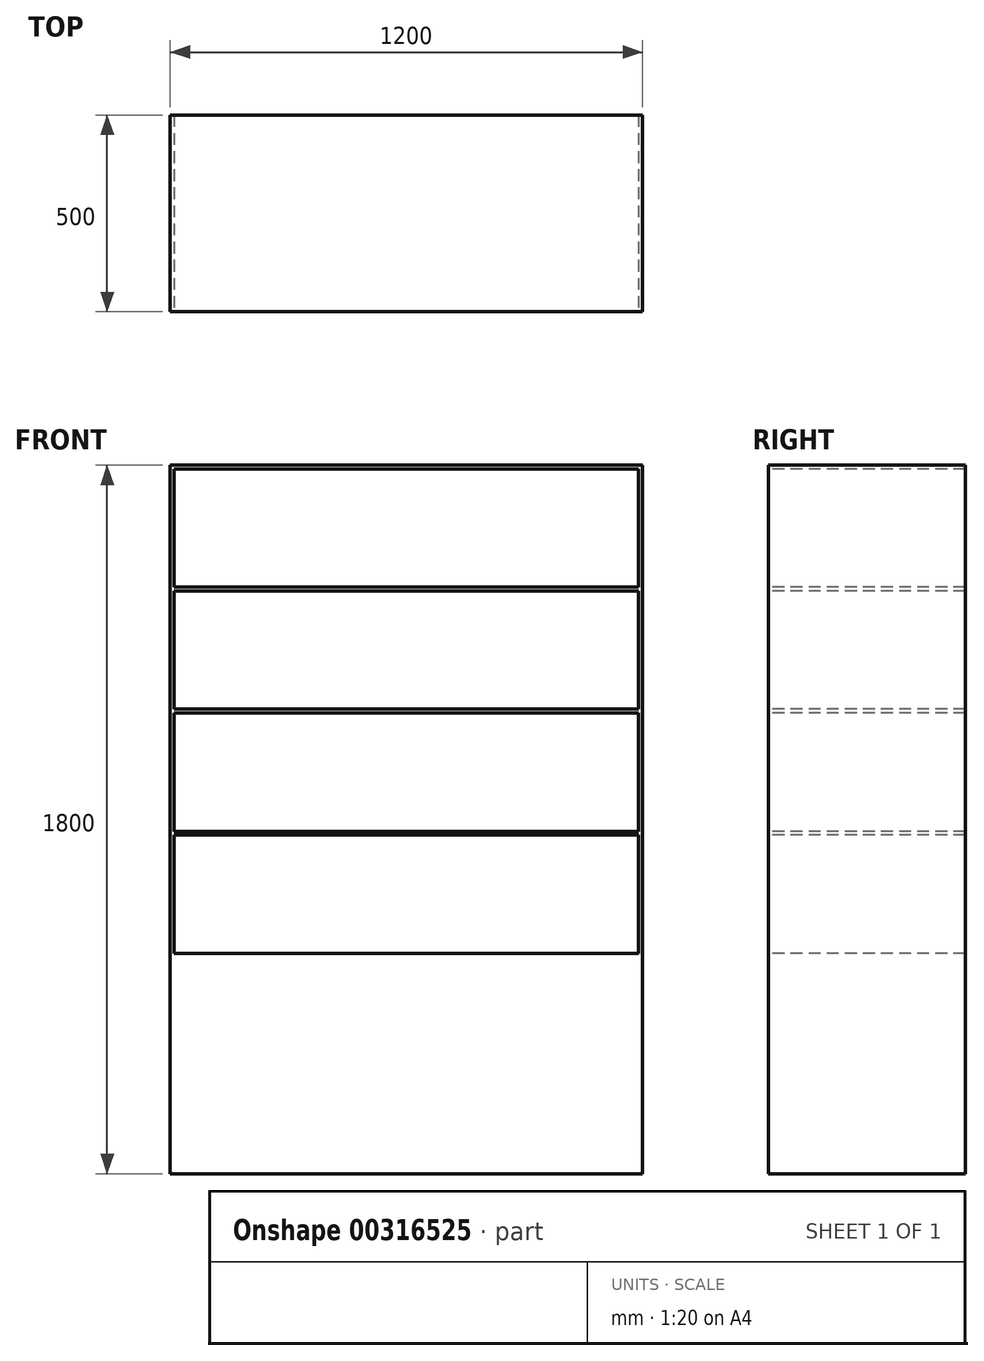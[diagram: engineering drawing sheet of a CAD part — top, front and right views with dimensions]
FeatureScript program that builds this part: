
annotation { "Feature Type Name" : "Feature", "Feature Type Description" : "" }
export const myFeature = defineFeature(function(context is Context, id is Id, definition is map)
    precondition{}
    {
        {
            var Q0;
            Q0=qCreatedBy(makeId("Front.planeOp"),FACE);
            var sketch = newSketch(context, id + "F0", { "sketchPlane" : qUnion([Q0])});
            skLineSegment(sketch, "E0.bottom", {"start": v(-1200, 1800) * mm, "end": v(0, 1800) * mm});
            skLineSegment(sketch, "E0.top", {"start": v(-1200, 0) * mm, "end": v(0, 0) * mm});
            skLineSegment(sketch, "E0.left", {"start": v(-1200, 1800) * mm, "end": v(-1200, 0) * mm});
            skLineSegment(sketch, "E0.right", {"start": v(0, 1800) * mm, "end": v(0, 0) * mm});
            skSolve(sketch);
        }
        {
            var Q0;
            Q0 = qSketchRegion(id + "F0", true);
            extrude(context, id + "F1", {"entities" : qUnion([Q0]), "depth" : 500 * mm});
        }
        {
            var Q0;
            Q0=makeQuery(id+"F1.opExtrude","CAP_FACE",FACE,{"disambiguationData":[OSD([sQuery(id+"F0.wireOp",EDGE,"E0.bottom"),sQuery(id+"F0.wireOp",EDGE,"E0.top"),sQuery(id+"F0.wireOp",EDGE,"E0.left"),sQuery(id+"F0.wireOp",EDGE,"E0.right")])],"isStart":false});
            var sketch = newSketch(context, id + "F2", { "sketchPlane" : qUnion([Q0])});
            skLineSegment(sketch, "E1.bottom", {"start": v(-1190, 1790) * mm, "end": v(-10, 1790) * mm});
            skLineSegment(sketch, "E1.top", {"start": v(-1190, 1490) * mm, "end": v(-10, 1490) * mm});
            skLineSegment(sketch, "E1.left", {"start": v(-1190, 1790) * mm, "end": v(-1190, 1490) * mm});
            skLineSegment(sketch, "E1.right", {"start": v(-10, 1790) * mm, "end": v(-10, 1490) * mm});
            skLineSegment(sketch, "E2.bottom", {"start": v(-1190, 1480) * mm, "end": v(-10, 1480) * mm});
            skLineSegment(sketch, "E2.top", {"start": v(-1190, 1180) * mm, "end": v(-10, 1180) * mm});
            skLineSegment(sketch, "E2.left", {"start": v(-1190, 1480) * mm, "end": v(-1190, 1180) * mm});
            skLineSegment(sketch, "E2.right", {"start": v(-10, 1480) * mm, "end": v(-10, 1180) * mm});
            skLineSegment(sketch, "E3.bottom", {"start": v(-1190, 1170) * mm, "end": v(-10, 1170) * mm});
            skLineSegment(sketch, "E3.top", {"start": v(-1190, 870) * mm, "end": v(-10, 870) * mm});
            skLineSegment(sketch, "E3.left", {"start": v(-1190, 1170) * mm, "end": v(-1190, 870) * mm});
            skLineSegment(sketch, "E3.right", {"start": v(-10, 1170) * mm, "end": v(-10, 870) * mm});
            skLineSegment(sketch, "E4.bottom", {"start": v(-1190, 860) * mm, "end": v(-10, 860) * mm});
            skLineSegment(sketch, "E4.top", {"start": v(-1190, 560) * mm, "end": v(-10, 560) * mm});
            skLineSegment(sketch, "E4.left", {"start": v(-1190, 860) * mm, "end": v(-1190, 560) * mm});
            skLineSegment(sketch, "E4.right", {"start": v(-10, 860) * mm, "end": v(-10, 560) * mm});
            skSolve(sketch);
        }
        {
            var Q0;
            Q0 = qSketchRegion(id + "F2", true);
            extrude(context, id + "F3", {"entities" : qUnion([Q0]), "operationType" : NewBodyOperationType.REMOVE, "endBound" : BoundingType.UP_TO_NEXT, "oppositeDirection" : true, "depth" : 25 * mm});
        }
    });
